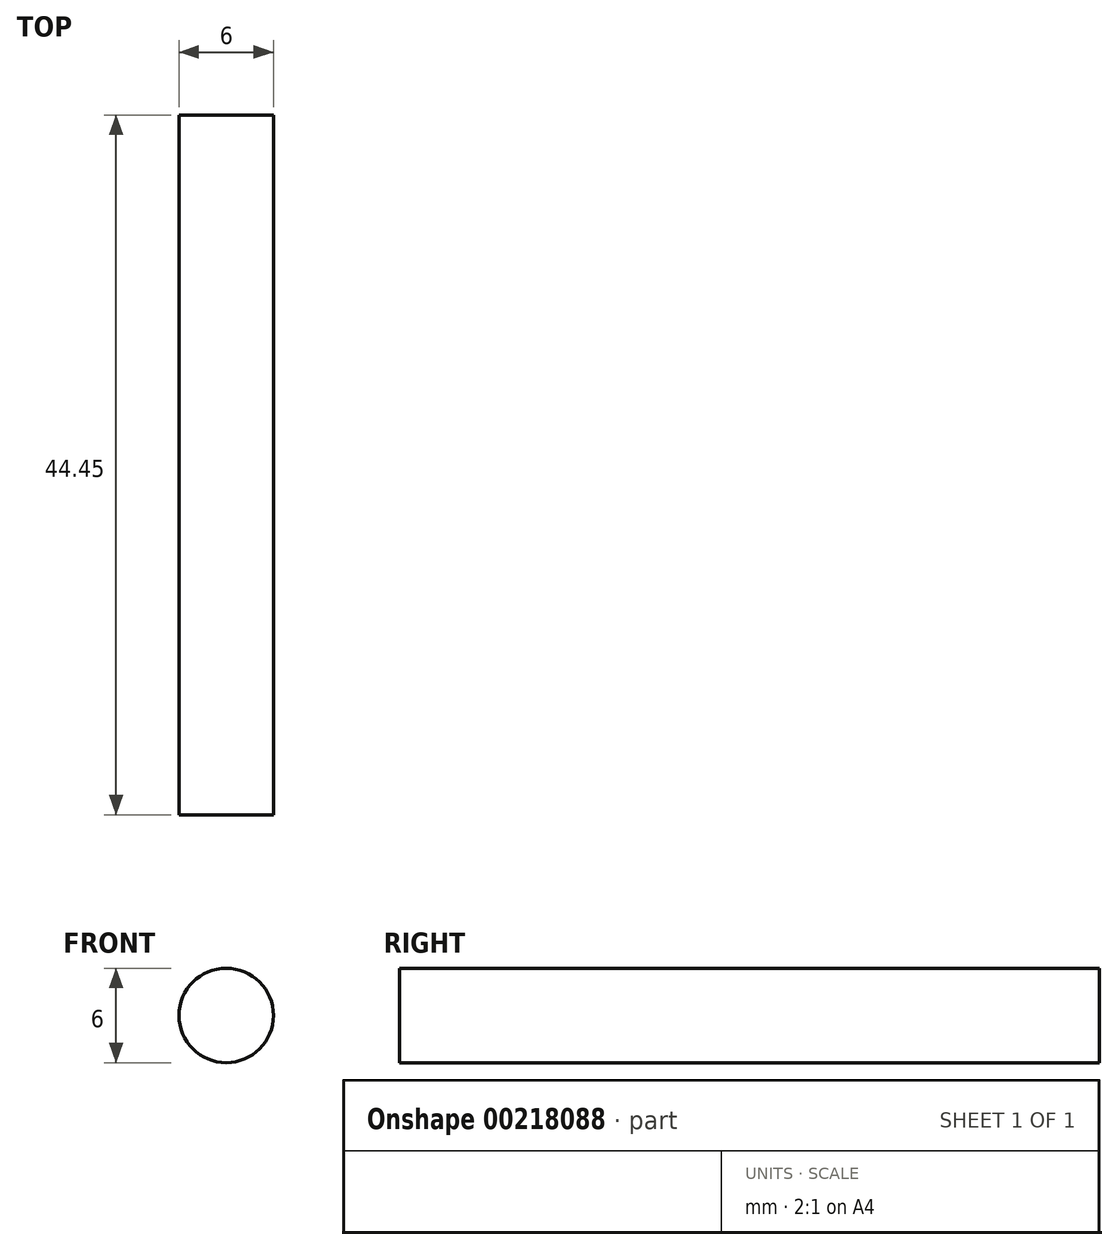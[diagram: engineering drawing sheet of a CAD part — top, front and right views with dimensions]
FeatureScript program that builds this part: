
annotation { "Feature Type Name" : "Feature", "Feature Type Description" : "" }
export const myFeature = defineFeature(function(context is Context, id is Id, definition is map)
    precondition{}
    {
        {
            var Q0;
            Q0=qCreatedBy(makeId("Front.planeOp"),FACE);
            var sketch = newSketch(context, id + "F0", { "sketchPlane" : qUnion([Q0])});
            skCircle(sketch, "E0", {"center": v(18.68, 12.5) * mm, "radius": 3 * mm});
            skSolve(sketch);
        }
        {
            var Q0;
            Q0=makeQuery(id+"F0.imprint","IMPRINT",FACE,{"disambiguationData":[TD([[makeQuery(id+"F0.imprint","IMPRINT",EDGE,{"derivedFrom":sQuery(id+"F0.wireOp",EDGE,"E0")}),1.0]])]});
            extrude(context, id + "F1", {"entities" : qUnion([Q0]), "depth" : 44.45 * mm});
        }
    });
